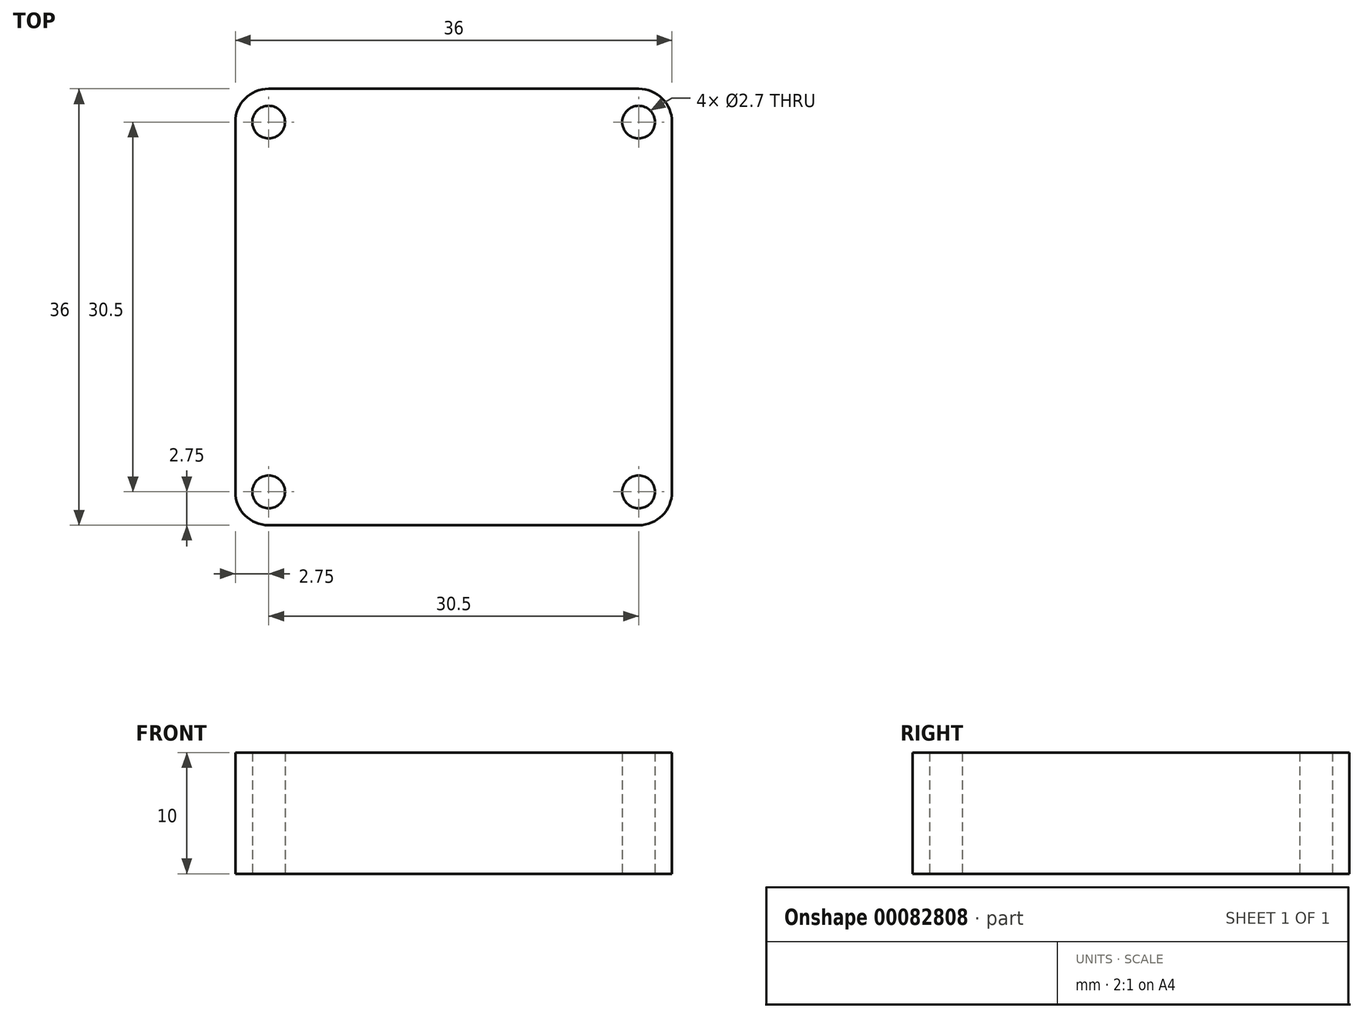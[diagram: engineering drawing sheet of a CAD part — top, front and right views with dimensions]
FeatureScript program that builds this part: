
annotation { "Feature Type Name" : "Feature", "Feature Type Description" : "" }
export const myFeature = defineFeature(function(context is Context, id is Id, definition is map)
    precondition{}
    {
        {
            var Q0;
            Q0=qCreatedBy(makeId("Top.planeOp"),FACE);
            var sketch = newSketch(context, id + "F0", { "sketchPlane" : qUnion([Q0])});
            skLineSegment(sketch, "E0.bottom", {"start": v(18, -18) * mm, "end": v(-18, -18) * mm});
            skLineSegment(sketch, "E0.top", {"start": v(18, 18) * mm, "end": v(-18, 18) * mm});
            skLineSegment(sketch, "E0.left", {"start": v(18, -18) * mm, "end": v(18, 18) * mm});
            skLineSegment(sketch, "E0.right", {"start": v(-18, -18) * mm, "end": v(-18, 18) * mm});
            skPoint(sketch, "E0.middle", {"position": v(0, 0) * mm});
            skCircle(sketch, "E1", {"center": v(15.25, 15.25) * mm, "radius": 1.35 * mm});
            skCircle(sketch, "E2.MirrorC", {"center": v(-15.25, 15.25) * mm, "radius": 1.35 * mm});
            skCircle(sketch, "E3.MirrorC", {"center": v(15.25, -15.25) * mm, "radius": 1.35 * mm});
            skCircle(sketch, "E4.MirrorC", {"center": v(-15.25, -15.25) * mm, "radius": 1.35 * mm});
            skSolve(sketch);
        }
        {
            var Q0;
            Q0 = qSketchRegion(id + "F0", true);
            extrude(context, id + "F1", {"entities" : qUnion([Q0]), "depth" : 10 * mm});
        }
        {
            var Q0;
            Q0=makeQuery(id+"F1.opExtrude","SWEPT_EDGE",EDGE,{"disambiguationData":[OSD([sQuery(id+"F0.wireOp",EDGE,"E0.top"),sQuery(id+"F0.wireOp",EDGE,"E0.right")])]});
            var Q1;
            Q1=makeQuery(id+"F1.opExtrude","SWEPT_EDGE",EDGE,{"disambiguationData":[OSD([sQuery(id+"F0.wireOp",EDGE,"E0.top"),sQuery(id+"F0.wireOp",EDGE,"E0.left")])]});
            var Q2;
            Q2=makeQuery(id+"F1.opExtrude","SWEPT_EDGE",EDGE,{"disambiguationData":[OSD([sQuery(id+"F0.wireOp",EDGE,"E0.bottom"),sQuery(id+"F0.wireOp",EDGE,"E0.left")])]});
            var Q3;
            Q3=makeQuery(id+"F1.opExtrude","SWEPT_EDGE",EDGE,{"disambiguationData":[OSD([sQuery(id+"F0.wireOp",EDGE,"E0.bottom"),sQuery(id+"F0.wireOp",EDGE,"E0.right")])]});
            fillet(context, id + "F2", {"entities" : qUnion([Q0, Q1, Q2, Q3]), "radius" : 2.75 * mm, "tangentPropagation" : true, "allowEdgeOverflow" : false});
        }
    });
